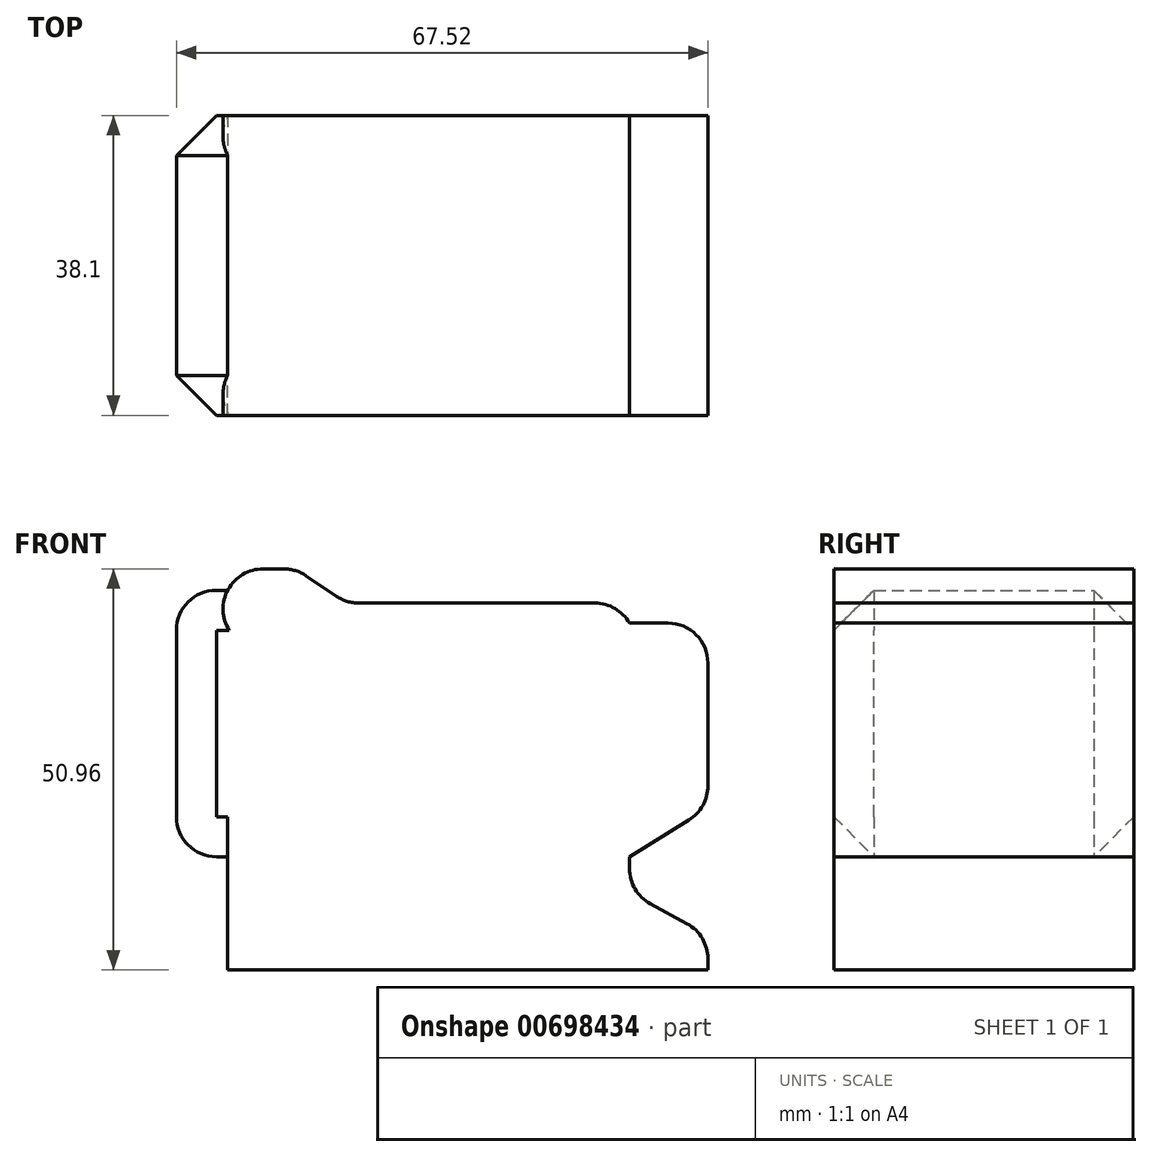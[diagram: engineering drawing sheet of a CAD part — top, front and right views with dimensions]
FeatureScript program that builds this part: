
annotation { "Feature Type Name" : "Feature", "Feature Type Description" : "" }
export const myFeature = defineFeature(function(context is Context, id is Id, definition is map)
    precondition{}
    {
        {
            var Q0;
            Q0=qCreatedBy(makeId("Front.planeOp"),FACE);
            var sketch = newSketch(context, id + "F0", { "sketchPlane" : qUnion([Q0])});
            skLineSegment(sketch, "E0", {"start": v(-15.12, 0) * mm, "end": v(45.89, 0) * mm});
            skLineSegment(sketch, "E1", {"start": v(45.89, 0) * mm, "end": v(45.89, 4.43) * mm});
            skLineSegment(sketch, "E2", {"start": v(45.89, 4.43) * mm, "end": v(35.93, 9.87) * mm});
            skLineSegment(sketch, "E3", {"start": v(35.93, 9.87) * mm, "end": v(35.93, 14.4) * mm});
            skLineSegment(sketch, "E4", {"start": v(35.93, 14.4) * mm, "end": v(45.89, 20.55) * mm});
            skLineSegment(sketch, "E5", {"start": v(45.89, 20.55) * mm, "end": v(45.89, 44.08) * mm});
            skLineSegment(sketch, "E6", {"start": v(45.89, 44.08) * mm, "end": v(35.93, 44.08) * mm});
            skLineSegment(sketch, "E7", {"start": v(35.93, 44.08) * mm, "end": v(35.93, 46.61) * mm});
            skLineSegment(sketch, "E8", {"start": v(35.93, 46.61) * mm, "end": v(0, 46.61) * mm});
            skLineSegment(sketch, "E9", {"start": v(0, 46.61) * mm, "end": v(-6.43, 50.96) * mm});
            skLineSegment(sketch, "E10", {"start": v(-6.43, 50.96) * mm, "end": v(-15.12, 50.96) * mm});
            skLineSegment(sketch, "E11", {"start": v(-15.12, 50.96) * mm, "end": v(-15.12, 48.24) * mm});
            skLineSegment(sketch, "E12", {"start": v(-15.12, 48.24) * mm, "end": v(-21.63, 48.24) * mm});
            skLineSegment(sketch, "E13", {"start": v(-21.63, 48.24) * mm, "end": v(-21.63, 14.4) * mm});
            skLineSegment(sketch, "E14", {"start": v(-21.63, 14.4) * mm, "end": v(-15.12, 14.4) * mm});
            skLineSegment(sketch, "E15", {"start": v(-15.12, 14.4) * mm, "end": v(-15.12, 4.43) * mm});
            skLineSegment(sketch, "E16", {"start": v(-15.12, 4.43) * mm, "end": v(-15.12, 0) * mm});
            skLineSegment(sketch, "E17", {"start": v(-6.43, 50.96) * mm, "end": v(-6.43, 4.43) * mm});
            skLineSegment(sketch, "E18", {"start": v(-6.43, 4.43) * mm, "end": v(-15.12, 4.43) * mm});
            skLineSegment(sketch, "E19", {"start": v(40.91, 44.08) * mm, "end": v(40.91, 17.47) * mm});
            skSolve(sketch);
        }
        {
            var Q0;
            Q0 = qSketchRegion(id + "F0", true);
            extrude(context, id + "F1", {"entities" : qUnion([Q0]), "depth" : 38.1 * mm, "offsetDistance" : 25.4 * mm});
        }
        {
            var Q0;
            Q0=makeQuery(id+"F1.opExtrude","SWEPT_EDGE",EDGE,{"disambiguationData":[OSD([sQuery(id+"F0.wireOp",EDGE,"E9"),sQuery(id+"F0.wireOp",EDGE,"E10"),sQuery(id+"F0.wireOp",EDGE,"E17")])]});
            var Q1;
            Q1=makeQuery(id+"F1.opExtrude","SWEPT_EDGE",EDGE,{"disambiguationData":[OSD([sQuery(id+"F0.wireOp",EDGE,"E8"),sQuery(id+"F0.wireOp",EDGE,"E9")])]});
            var Q2;
            Q2=makeQuery(id+"F1.opExtrude","SWEPT_EDGE",EDGE,{"disambiguationData":[OSD([sQuery(id+"F0.wireOp",EDGE,"E10"),sQuery(id+"F0.wireOp",EDGE,"E11")])]});
            var Q3;
            Q3=makeQuery(id+"F1.opExtrude","SWEPT_EDGE",EDGE,{"disambiguationData":[OSD([sQuery(id+"F0.wireOp",EDGE,"E7"),sQuery(id+"F0.wireOp",EDGE,"E8")])]});
            var Q4;
            Q4=makeQuery(id+"F1.opExtrude","SWEPT_EDGE",EDGE,{"disambiguationData":[OSD([sQuery(id+"F0.wireOp",EDGE,"E5"),sQuery(id+"F0.wireOp",EDGE,"E6")])]});
            var Q5;
            Q5=makeQuery(id+"F1.opExtrude","SWEPT_EDGE",EDGE,{"disambiguationData":[OSD([sQuery(id+"F0.wireOp",EDGE,"E4"),sQuery(id+"F0.wireOp",EDGE,"E5")])]});
            var Q6;
            Q6=makeQuery(id+"F1.opExtrude","SWEPT_EDGE",EDGE,{"disambiguationData":[OSD([sQuery(id+"F0.wireOp",EDGE,"E2"),sQuery(id+"F0.wireOp",EDGE,"E3")])]});
            var Q7;
            Q7=makeQuery(id+"F1.opExtrude","SWEPT_EDGE",EDGE,{"disambiguationData":[OSD([sQuery(id+"F0.wireOp",EDGE,"E1"),sQuery(id+"F0.wireOp",EDGE,"E2")])]});
            var Q8;
            Q8=makeQuery(id+"F1.opExtrude","SWEPT_EDGE",EDGE,{"disambiguationData":[OSD([sQuery(id+"F0.wireOp",EDGE,"E12"),sQuery(id+"F0.wireOp",EDGE,"E13")])]});
            var Q9;
            Q9=makeQuery(id+"F1.opExtrude","SWEPT_EDGE",EDGE,{"disambiguationData":[OSD([sQuery(id+"F0.wireOp",EDGE,"E13"),sQuery(id+"F0.wireOp",EDGE,"E14")])]});
            fillet(context, id + "F2", {"entities" : qUnion([Q0, Q1, Q2, Q3, Q4, Q5, Q6, Q7, Q8, Q9]), "radius" : 5.08 * mm, "tangentPropagation" : true, "allowEdgeOverflow" : false});
        }
        {
            var Q0;
            Q0=makeQuery(id+"F2.opFillet","BLEND_FACE",FACE,{"disambiguationData":[OSD([sQuery(id+"F0.wireOp",EDGE,"E12"),sQuery(id+"F0.wireOp",EDGE,"E13")])]});
            chamfer(context, id + "F3", {"entities" : qUnion([Q0]), "width" : 5.08 * mm, "tangentPropagation" : true});
        }
    });
